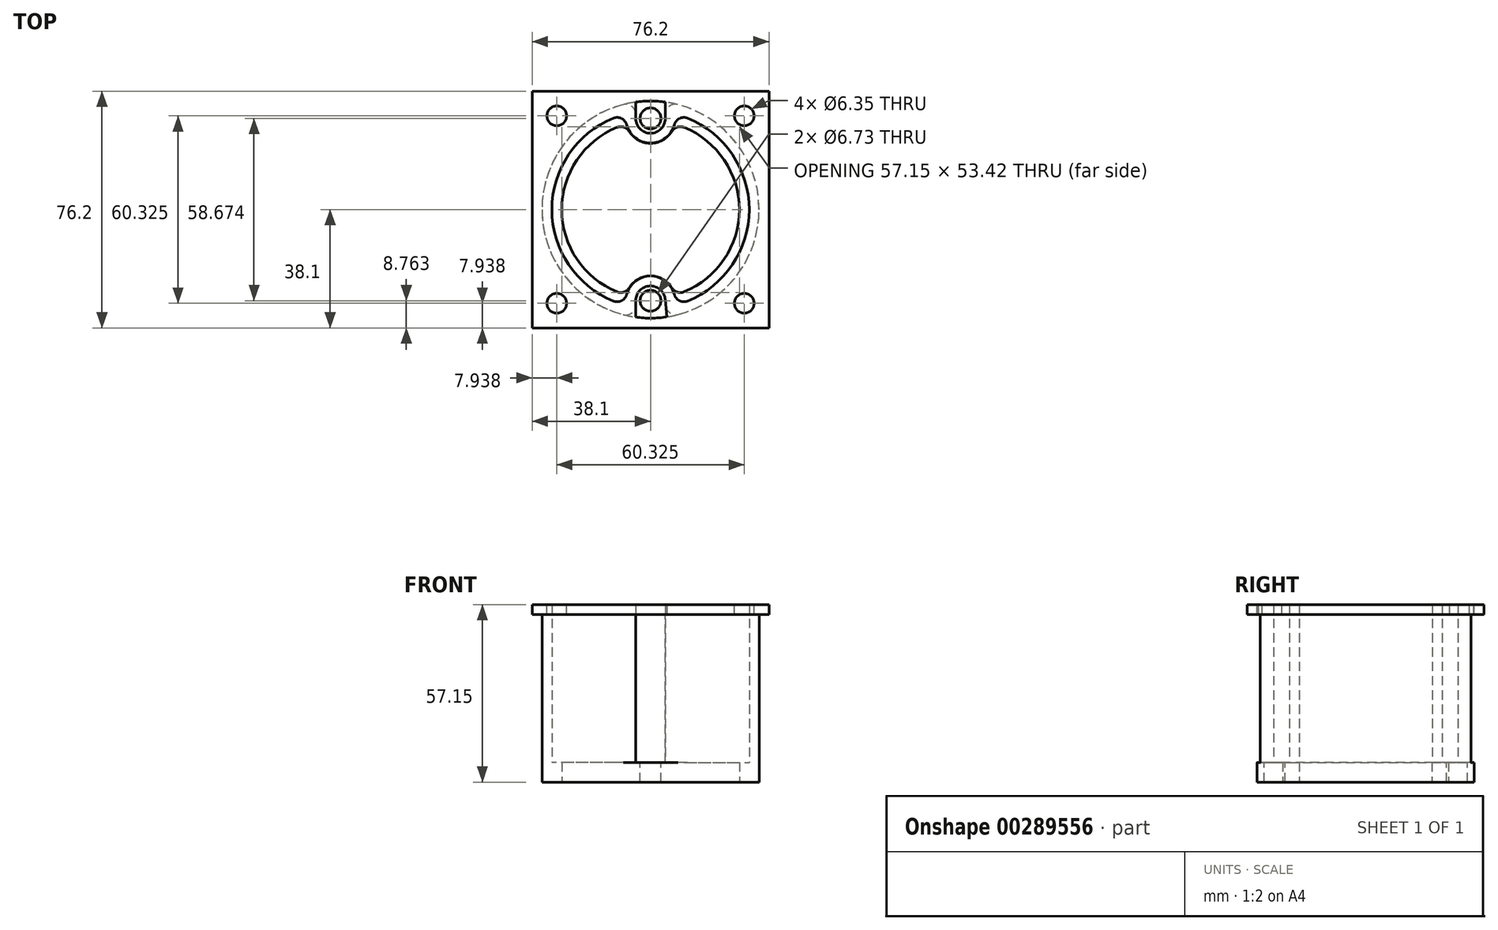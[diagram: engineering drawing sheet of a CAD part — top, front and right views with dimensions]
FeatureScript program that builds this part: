
annotation { "Feature Type Name" : "Feature", "Feature Type Description" : "" }
export const myFeature = defineFeature(function(context is Context, id is Id, definition is map)
    precondition{}
    {
        {
            var Q0;
            Q0=qCreatedBy(makeId("Top.planeOp"),FACE);
            var sketch = newSketch(context, id + "F0", { "sketchPlane" : qUnion([Q0])});
            skCircle(sketch, "E0", {"center": v(0, 0) * mm, "radius": 34.93 * mm});
            skSolve(sketch);
        }
        {
            var Q0;
            Q0 = qSketchRegion(id + "F0", true);
            extrude(context, id + "F1", {"entities" : qUnion([Q0]), "depth" : 6.35 * mm});
        }
        {
            var Q0;
            Q0=makeQuery(id+"F1.opExtrude","CAP_FACE",FACE,{"disambiguationData":[OSD([sQuery(id+"F0.wireOp",EDGE,"E0")])],"isStart":false});
            var sketch = newSketch(context, id + "F2", { "sketchPlane" : qUnion([Q0])});
            skCircle(sketch, "E1", {"center": v(0, 0) * mm, "radius": 29.34 * mm, "construction": true});
            skArc(sketch, "E2", {"start": v(-4.76, 29.34) * mm, "mid": v(0, 24.57) * mm, "end": v(4.76, 29.34) * mm});
            skArc(sketch, "E3", {"start": v(4.75, -28.95) * mm, "mid": v(-0.2, -24.58) * mm, "end": v(-4.76, -29.34) * mm});
            skLineSegment(sketch, "E4", {"start": v(-4.76, 29.34) * mm, "end": v(-4.76, 34.6) * mm});
            skLineSegment(sketch, "E5", {"start": v(4.76, 29.34) * mm, "end": v(4.76, 34.6) * mm});
            skLineSegment(sketch, "E6", {"start": v(-4.76, -29.34) * mm, "end": v(-4.76, -34.6) * mm});
            skLineSegment(sketch, "E7", {"start": v(4.75, -28.95) * mm, "end": v(5.2, -34.54) * mm});
            skArc(sketch, "E8", {"start": v(5.2, -34.54) * mm, "mid": v(34.92, 0.22) * mm, "end": v(4.76, 34.6) * mm});
            skArc(sketch, "E9.0", {"start": v(-7.94, 30.74) * mm, "mid": v(-31.75, 0) * mm, "end": v(-7.94, -30.74) * mm});
            skArc(sketch, "E10.0", {"start": v(-7.94, 29.34) * mm, "mid": v(0, 21.4) * mm, "end": v(7.94, 29.34) * mm});
            skArc(sketch, "E11.0", {"start": v(7.91, -28.7) * mm, "mid": v(-0.32, -21.4) * mm, "end": v(-7.94, -29.34) * mm});
            skLineSegment(sketch, "E12.0", {"start": v(7.94, 29.34) * mm, "end": v(7.94, 30.74) * mm});
            skLineSegment(sketch, "E13.0", {"start": v(-7.94, 29.34) * mm, "end": v(-7.94, 30.74) * mm});
            skLineSegment(sketch, "E14.0", {"start": v(7.91, -28.7) * mm, "end": v(8.08, -30.7) * mm});
            skLineSegment(sketch, "E15.0", {"start": v(-7.94, -29.34) * mm, "end": v(-7.94, -30.74) * mm});
            skArc(sketch, "E16.trimOffspring", {"start": v(8.08, -30.7) * mm, "mid": v(31.75, 0.07) * mm, "end": v(7.94, 30.74) * mm});
            skArc(sketch, "E17.trimOffspring", {"start": v(-4.76, 34.6) * mm, "mid": v(-34.93, 0) * mm, "end": v(-4.76, -34.6) * mm});
            skSolve(sketch);
        }
        {
            var Q0;
            Q0=makeQuery(id+"F2.imprint","IMPRINT",FACE,{"disambiguationData":[TD([[makeQuery(id+"F2.imprint","IMPRINT",EDGE,{"derivedFrom":sQuery(id+"F2.wireOp",EDGE,"E2")}),-1.0]])]});
            extrude(context, id + "F3", {"entities" : qUnion([Q0]), "operationType" : NewBodyOperationType.ADD, "depth" : 50.8 * mm});
        }
        {
            var Q0;
            Q0=makeQuery(id+"F3.boolean.opBoolean","SPLIT",FACE,{"disambiguationData":[TD([makeQuery(id+"F3.opExtrude","SWEPT_FACE",FACE,{"disambiguationData":[OSD([sQuery(id+"F2.wireOp",EDGE,"E9.0")])]})])],"derivedFrom":makeQuery(id+"F1.opExtrude","CAP_FACE",FACE,{"disambiguationData":[OSD([sQuery(id+"F0.wireOp",EDGE,"E0")])],"isStart":false})});
            var sketch = newSketch(context, id + "F4", { "sketchPlane" : qUnion([Q0])});
            skCircle(sketch, "E18", {"center": v(0, 29.34) * mm, "radius": 3.37 * mm});
            skCircle(sketch, "E19", {"center": v(0, -29.34) * mm, "radius": 3.37 * mm});
            skSolve(sketch);
        }
        {
            var Q0;
            Q0 = qSketchRegion(id + "F4", true);
            extrude(context, id + "F5", {"entities" : qUnion([Q0]), "operationType" : NewBodyOperationType.REMOVE, "endBound" : BoundingType.UP_TO_NEXT, "oppositeDirection" : true, "depth" : 25.4 * mm});
        }
        {
            var Q0;
            Q0=makeQuery(id+"F3.opExtrude","CAP_FACE",FACE,{"disambiguationData":[OSD([sQuery(id+"F2.wireOp",EDGE,"E2"),sQuery(id+"F2.wireOp",EDGE,"E3"),sQuery(id+"F2.wireOp",EDGE,"E4"),sQuery(id+"F2.wireOp",EDGE,"E5"),sQuery(id+"F2.wireOp",EDGE,"E6"),sQuery(id+"F2.wireOp",EDGE,"E7"),sQuery(id+"F2.wireOp",EDGE,"E8"),sQuery(id+"F2.wireOp",EDGE,"E9.0"),sQuery(id+"F2.wireOp",EDGE,"E10.0"),sQuery(id+"F2.wireOp",EDGE,"E11.0"),sQuery(id+"F2.wireOp",EDGE,"E12.0"),sQuery(id+"F2.wireOp",EDGE,"E13.0"),sQuery(id+"F2.wireOp",EDGE,"E14.0"),sQuery(id+"F2.wireOp",EDGE,"E15.0"),sQuery(id+"F2.wireOp",EDGE,"E16.trimOffspring"),sQuery(id+"F2.wireOp",EDGE,"E17.trimOffspring")])],"isStart":false});
            var sketch = newSketch(context, id + "F6", { "sketchPlane" : qUnion([Q0])});
            skLineSegment(sketch, "E20.bottom", {"start": v(38.1, 38.1) * mm, "end": v(-38.1, 38.1) * mm});
            skLineSegment(sketch, "E20.top", {"start": v(38.1, -38.1) * mm, "end": v(-38.1, -38.1) * mm});
            skLineSegment(sketch, "E20.left", {"start": v(38.1, 38.1) * mm, "end": v(38.1, -38.1) * mm});
            skLineSegment(sketch, "E20.right", {"start": v(-38.1, 38.1) * mm, "end": v(-38.1, -38.1) * mm});
            skPoint(sketch, "E20.middle", {"position": v(0, 0) * mm});
            skCircle(sketch, "E21", {"center": v(0, 0) * mm, "radius": 34.93 * mm});
            skSolve(sketch);
        }
        {
            var Q0;
            Q0 = qSketchRegion(id + "F6", true);
            extrude(context, id + "F7", {"entities" : qUnion([Q0]), "operationType" : NewBodyOperationType.ADD, "oppositeDirection" : true, "depth" : 3.17 * mm});
        }
        {
            var Q0;
            Q0=makeQuery(id+"F7.boolean.opBoolean","MERGE",FACE,{"derivedFrom":[makeQuery(id+"F3.opExtrude","CAP_FACE",FACE,{"disambiguationData":[OSD([sQuery(id+"F2.wireOp",EDGE,"E2"),sQuery(id+"F2.wireOp",EDGE,"E3"),sQuery(id+"F2.wireOp",EDGE,"E4"),sQuery(id+"F2.wireOp",EDGE,"E5"),sQuery(id+"F2.wireOp",EDGE,"E6"),sQuery(id+"F2.wireOp",EDGE,"E7"),sQuery(id+"F2.wireOp",EDGE,"E8"),sQuery(id+"F2.wireOp",EDGE,"E9.0"),sQuery(id+"F2.wireOp",EDGE,"E10.0"),sQuery(id+"F2.wireOp",EDGE,"E11.0"),sQuery(id+"F2.wireOp",EDGE,"E12.0"),sQuery(id+"F2.wireOp",EDGE,"E13.0"),sQuery(id+"F2.wireOp",EDGE,"E14.0"),sQuery(id+"F2.wireOp",EDGE,"E15.0"),sQuery(id+"F2.wireOp",EDGE,"E16.trimOffspring"),sQuery(id+"F2.wireOp",EDGE,"E17.trimOffspring")])],"isStart":false}),makeQuery(id+"F7.opExtrude","CAP_FACE",FACE,{"disambiguationData":[OSD([sQuery(id+"F6.wireOp",EDGE,"E20.bottom"),sQuery(id+"F6.wireOp",EDGE,"E20.top"),sQuery(id+"F6.wireOp",EDGE,"E20.left"),sQuery(id+"F6.wireOp",EDGE,"E20.right"),sQuery(id+"F6.wireOp",EDGE,"E21")])],"isStart":true})]});
            var sketch = newSketch(context, id + "F8", { "sketchPlane" : qUnion([Q0])});
            skLineSegment(sketch, "E22.bottom", {"start": v(30.16, 30.16) * mm, "end": v(-30.16, 30.16) * mm, "construction": true});
            skLineSegment(sketch, "E22.top", {"start": v(30.16, -30.16) * mm, "end": v(-30.16, -30.16) * mm, "construction": true});
            skLineSegment(sketch, "E22.left", {"start": v(30.16, 30.16) * mm, "end": v(30.16, -30.16) * mm, "construction": true});
            skLineSegment(sketch, "E22.right", {"start": v(-30.16, 30.16) * mm, "end": v(-30.16, -30.16) * mm, "construction": true});
            skPoint(sketch, "E22.middle", {"position": v(0, 0) * mm});
            skCircle(sketch, "E23", {"center": v(-30.16, 30.16) * mm, "radius": 3.18 * mm});
            skCircle(sketch, "E24", {"center": v(30.16, 30.16) * mm, "radius": 3.18 * mm});
            skCircle(sketch, "E25", {"center": v(-30.16, -30.16) * mm, "radius": 3.18 * mm});
            skCircle(sketch, "E26", {"center": v(30.16, -30.16) * mm, "radius": 3.18 * mm});
            skSolve(sketch);
        }
        {
            var Q0;
            Q0 = qSketchRegion(id + "F8", true);
            extrude(context, id + "F9", {"entities" : qUnion([Q0]), "operationType" : NewBodyOperationType.REMOVE, "endBound" : BoundingType.UP_TO_NEXT, "oppositeDirection" : true, "depth" : 25.4 * mm});
        }
        {
            var Q0;
            {var subQ0=sQuery(id+"F0.wireOp",EDGE,"E0");var subQ1=sQuery(id+"F2.wireOp",EDGE,"E17.trimOffspring");var subQ2=sQuery(id+"F2.wireOp",EDGE,"E6");Q0=makeQuery(id+"F7.boolean.opBoolean","SPLIT",EDGE,{"disambiguationData":[topologyDisambiguationEdgeConnected([makeQuery(id+"F1.opExtrude","SWEPT_FACE",FACE,{"disambiguationData":[OSD([subQ0])]})])],"derivedFrom":makeQuery(id+"F3.opExtrude","SWEPT_EDGE",EDGE,{"disambiguationData":[OSD([subQ0,subQ2,subQ1])]})});}
            var Q1;
            {var subQ0=sQuery(id+"F0.wireOp",EDGE,"E0");var subQ1=sQuery(id+"F2.wireOp",EDGE,"E7");var subQ2=sQuery(id+"F2.wireOp",EDGE,"E8");Q1=makeQuery(id+"F7.boolean.opBoolean","SPLIT",EDGE,{"disambiguationData":[topologyDisambiguationEdgeConnected([makeQuery(id+"F1.opExtrude","SWEPT_FACE",FACE,{"disambiguationData":[OSD([subQ0])]})])],"derivedFrom":makeQuery(id+"F3.opExtrude","SWEPT_EDGE",EDGE,{"disambiguationData":[OSD([subQ0,subQ1,subQ2])]})});}
            var Q2;
            {var subQ0=sQuery(id+"F0.wireOp",EDGE,"E0");var subQ1=sQuery(id+"F2.wireOp",EDGE,"E5");var subQ2=sQuery(id+"F2.wireOp",EDGE,"E8");Q2=makeQuery(id+"F7.boolean.opBoolean","SPLIT",EDGE,{"disambiguationData":[topologyDisambiguationEdgeConnected([makeQuery(id+"F1.opExtrude","SWEPT_FACE",FACE,{"disambiguationData":[OSD([subQ0])]})])],"derivedFrom":makeQuery(id+"F3.opExtrude","SWEPT_EDGE",EDGE,{"disambiguationData":[OSD([subQ0,subQ1,subQ2])]})});}
            var Q3;
            {var subQ0=sQuery(id+"F0.wireOp",EDGE,"E0");var subQ1=sQuery(id+"F2.wireOp",EDGE,"E17.trimOffspring");var subQ2=sQuery(id+"F2.wireOp",EDGE,"E4");Q3=makeQuery(id+"F7.boolean.opBoolean","SPLIT",EDGE,{"disambiguationData":[topologyDisambiguationEdgeConnected([makeQuery(id+"F1.opExtrude","SWEPT_FACE",FACE,{"disambiguationData":[OSD([subQ0])]})])],"derivedFrom":makeQuery(id+"F3.opExtrude","SWEPT_EDGE",EDGE,{"disambiguationData":[OSD([subQ0,subQ2,subQ1])]})});}
            var Q4;
            Q4=makeQuery(id+"F3.opExtrude","SWEPT_EDGE",EDGE,{"disambiguationData":[OSD([sQuery(id+"F2.wireOp",EDGE,"E9.0"),sQuery(id+"F2.wireOp",EDGE,"E15.0")])]});
            var Q5;
            Q5=makeQuery(id+"F3.opExtrude","SWEPT_EDGE",EDGE,{"disambiguationData":[OSD([sQuery(id+"F2.wireOp",EDGE,"E14.0"),sQuery(id+"F2.wireOp",EDGE,"E16.trimOffspring")])]});
            var Q6;
            Q6=makeQuery(id+"F3.opExtrude","SWEPT_EDGE",EDGE,{"disambiguationData":[OSD([sQuery(id+"F2.wireOp",EDGE,"E9.0"),sQuery(id+"F2.wireOp",EDGE,"E13.0")])]});
            var Q7;
            Q7=makeQuery(id+"F3.opExtrude","SWEPT_EDGE",EDGE,{"disambiguationData":[OSD([sQuery(id+"F2.wireOp",EDGE,"E12.0"),sQuery(id+"F2.wireOp",EDGE,"E16.trimOffspring")])]});
            fillet(context, id + "F10", {"entities" : qUnion([Q0, Q1, Q2, Q3, Q4, Q5, Q6, Q7]), "radius" : 3.17 * mm, "tangentPropagation" : true, "allowEdgeOverflow" : false});
        }
        {
            var Q0;
            Q0=qCreatedBy(makeId("Top.planeOp"),FACE);
            var sketch = newSketch(context, id + "F11", { "sketchPlane" : qUnion([Q0])});
            skArc(sketch, "E27", {"start": v(-7.79, 27.5) * mm, "mid": v(-28.58, 0) * mm, "end": v(-7.79, -27.5) * mm});
            skArc(sketch, "E28", {"start": v(7.79, -27.5) * mm, "mid": v(0, -21.34) * mm, "end": v(-7.79, -27.5) * mm});
            skArc(sketch, "E29", {"start": v(-7.79, 27.5) * mm, "mid": v(0, 21.34) * mm, "end": v(7.79, 27.5) * mm});
            skArc(sketch, "E30.trimOffspring", {"start": v(7.79, -27.5) * mm, "mid": v(28.58, 0) * mm, "end": v(7.79, 27.5) * mm});
            skSolve(sketch);
        }
        {
            var Q0;
            Q0 = qSketchRegion(id + "F11", true);
            extrude(context, id + "F12", {"entities" : qUnion([Q0]), "operationType" : NewBodyOperationType.REMOVE, "endBound" : BoundingType.UP_TO_NEXT, "depth" : 25.4 * mm});
        }
        {
            var Q0;
            Q0=makeQuery(id+"F12.boolean.opBoolean","COPY",EDGE,{"derivedFrom":makeQuery(id+"F12.opExtrude","SWEPT_EDGE",EDGE,{"disambiguationData":[OSD([sQuery(id+"F11.wireOp",EDGE,"E27"),sQuery(id+"F11.wireOp",EDGE,"E29")])]})});
            var Q1;
            Q1=makeQuery(id+"F12.boolean.opBoolean","COPY",EDGE,{"derivedFrom":makeQuery(id+"F12.opExtrude","SWEPT_EDGE",EDGE,{"disambiguationData":[OSD([sQuery(id+"F11.wireOp",EDGE,"E29"),sQuery(id+"F11.wireOp",EDGE,"E30.trimOffspring")])]})});
            var Q2;
            Q2=makeQuery(id+"F12.boolean.opBoolean","COPY",EDGE,{"derivedFrom":makeQuery(id+"F12.opExtrude","SWEPT_EDGE",EDGE,{"disambiguationData":[OSD([sQuery(id+"F11.wireOp",EDGE,"E27"),sQuery(id+"F11.wireOp",EDGE,"E28")])]})});
            var Q3;
            Q3=makeQuery(id+"F12.boolean.opBoolean","COPY",EDGE,{"derivedFrom":makeQuery(id+"F12.opExtrude","SWEPT_EDGE",EDGE,{"disambiguationData":[OSD([sQuery(id+"F11.wireOp",EDGE,"E28"),sQuery(id+"F11.wireOp",EDGE,"E30.trimOffspring")])]})});
            fillet(context, id + "F13", {"entities" : qUnion([Q0, Q1, Q2, Q3]), "radius" : 3.17 * mm, "tangentPropagation" : true, "allowEdgeOverflow" : false});
        }
    });
